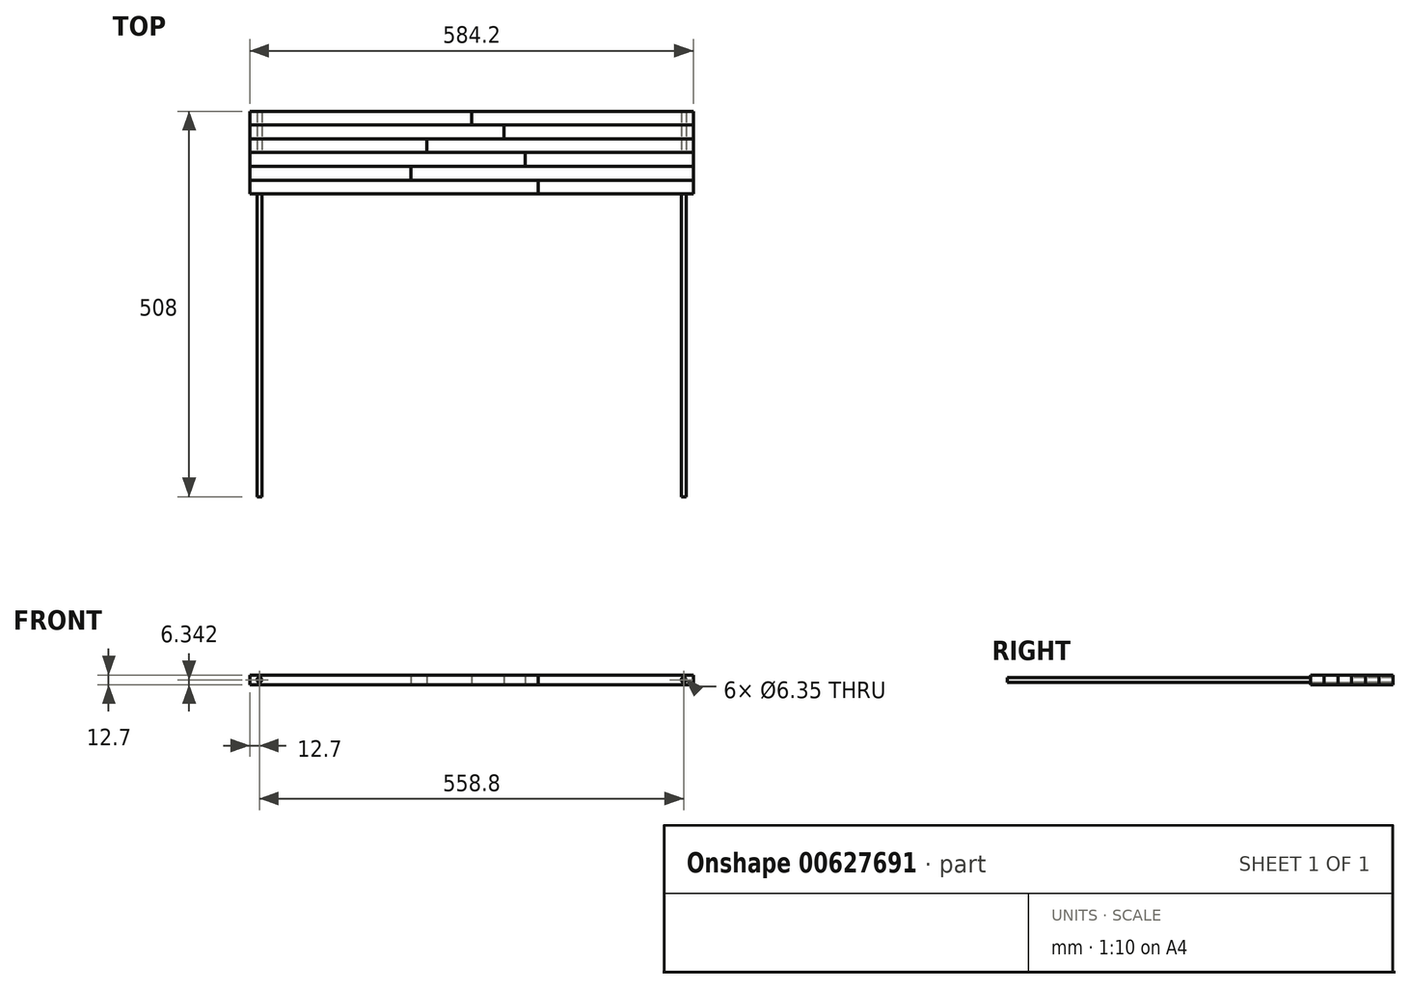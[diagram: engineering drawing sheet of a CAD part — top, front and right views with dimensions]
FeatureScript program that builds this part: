
annotation { "Feature Type Name" : "Feature", "Feature Type Description" : "" }
export const myFeature = defineFeature(function(context is Context, id is Id, definition is map)
    precondition{}
    {
        {
            var Q0;
            Q0=qCreatedBy(makeId("Top.planeOp"),FACE);
            var sketch = newSketch(context, id + "F0", { "sketchPlane" : qUnion([Q0])});
            skLineSegment(sketch, "E0.bottom", {"start": v(292.1, 254) * mm, "end": v(-292.1, 254) * mm});
            skLineSegment(sketch, "E0.top", {"start": v(292.1, -254) * mm, "end": v(-292.1, -254) * mm});
            skLineSegment(sketch, "E0.left", {"start": v(292.1, 254) * mm, "end": v(292.1, -254) * mm});
            skLineSegment(sketch, "E0.right", {"start": v(-292.1, 254) * mm, "end": v(-292.1, -254) * mm});
            skPoint(sketch, "E0.middle", {"position": v(0, 0) * mm});
            skLineSegment(sketch, "E1.1.0.0", {"start": v(292.1, 235.86) * mm, "end": v(-292.1, 235.86) * mm});
            skLineSegment(sketch, "E1.2.0.0", {"start": v(292.1, 217.71) * mm, "end": v(-292.1, 217.71) * mm});
            skLineSegment(sketch, "E1.3.0.0", {"start": v(292.1, 199.57) * mm, "end": v(-292.1, 199.57) * mm});
            skLineSegment(sketch, "E1.4.0.0", {"start": v(292.1, 181.43) * mm, "end": v(-292.1, 181.43) * mm});
            skLineSegment(sketch, "E1.5.0.0", {"start": v(292.1, 163.29) * mm, "end": v(-292.1, 163.29) * mm});
            skLineSegment(sketch, "E1.6.0.0", {"start": v(292.1, 145.14) * mm, "end": v(-292.1, 145.14) * mm});
            skLineSegment(sketch, "E1.7.0.0", {"start": v(292.1, 127) * mm, "end": v(-292.1, 127) * mm});
            skLineSegment(sketch, "E1.8.0.0", {"start": v(292.1, 108.86) * mm, "end": v(-292.1, 108.86) * mm});
            skLineSegment(sketch, "E1.9.0.0", {"start": v(292.1, 90.71) * mm, "end": v(-292.1, 90.71) * mm});
            skLineSegment(sketch, "E1.10.0.0", {"start": v(292.1, 72.57) * mm, "end": v(-292.1, 72.57) * mm});
            skLineSegment(sketch, "E1.11.0.0", {"start": v(292.1, 54.43) * mm, "end": v(-292.1, 54.43) * mm});
            skLineSegment(sketch, "E1.12.0.0", {"start": v(292.1, 36.29) * mm, "end": v(-292.1, 36.29) * mm});
            skLineSegment(sketch, "E1.13.0.0", {"start": v(292.1, 18.14) * mm, "end": v(-292.1, 18.14) * mm});
            skLineSegment(sketch, "E1.14.0.0", {"start": v(292.1, 0) * mm, "end": v(-292.1, 0) * mm});
            skLineSegment(sketch, "E1.15.0.0", {"start": v(292.1, -18.14) * mm, "end": v(-292.1, -18.14) * mm});
            skLineSegment(sketch, "E1.16.0.0", {"start": v(292.1, -36.29) * mm, "end": v(-292.1, -36.29) * mm});
            skLineSegment(sketch, "E1.17.0.0", {"start": v(292.1, -54.43) * mm, "end": v(-292.1, -54.43) * mm});
            skLineSegment(sketch, "E1.18.0.0", {"start": v(292.1, -72.57) * mm, "end": v(-292.1, -72.57) * mm});
            skLineSegment(sketch, "E1.19.0.0", {"start": v(292.1, -90.71) * mm, "end": v(-292.1, -90.71) * mm});
            skLineSegment(sketch, "E1.20.0.0", {"start": v(292.1, -108.86) * mm, "end": v(-292.1, -108.86) * mm});
            skLineSegment(sketch, "E1.21.0.0", {"start": v(292.1, -127) * mm, "end": v(-292.1, -127) * mm});
            skLineSegment(sketch, "E1.22.0.0", {"start": v(292.1, -145.14) * mm, "end": v(-292.1, -145.14) * mm});
            skLineSegment(sketch, "E1.23.0.0", {"start": v(292.1, -163.29) * mm, "end": v(-292.1, -163.29) * mm});
            skLineSegment(sketch, "E1.24.0.0", {"start": v(292.1, -181.43) * mm, "end": v(-292.1, -181.43) * mm});
            skLineSegment(sketch, "E1.25.0.0", {"start": v(292.1, -199.57) * mm, "end": v(-292.1, -199.57) * mm});
            skLineSegment(sketch, "E1.26.0.0", {"start": v(292.1, -217.71) * mm, "end": v(-292.1, -217.71) * mm});
            skLineSegment(sketch, "E1.27.0.0", {"start": v(292.1, -235.86) * mm, "end": v(-292.1, -235.86) * mm});
            skLineSegment(sketch, "E1.direction1", {"start": v(-292.1, 254) * mm, "end": v(-292.1, 235.86) * mm, "construction": true});
            skEllipse(sketch, "E2", {"center": v(0, 0) * mm, "majorRadius": 254 * mm, "minorRadius": 114.3 * mm, "majorAxis": v(0, 1), "construction": true});
            skLineSegment(sketch, "E3", {"start": v(0, 254) * mm, "end": v(0, 235.86) * mm});
            skLineSegment(sketch, "E4", {"start": v(42.42, 235.86) * mm, "end": v(42.42, 217.71) * mm});
            skLineSegment(sketch, "E5", {"start": v(-58.87, 217.71) * mm, "end": v(-58.87, 199.57) * mm});
            skLineSegment(sketch, "E6", {"start": v(70.7, 199.57) * mm, "end": v(70.7, 181.43) * mm});
            skLineSegment(sketch, "E7", {"start": v(-80, 181.43) * mm, "end": v(-80, 163.29) * mm});
            skLineSegment(sketch, "E8", {"start": v(87.55, 163.29) * mm, "end": v(87.55, 145.14) * mm});
            skLineSegment(sketch, "E9", {"start": v(-93.8, 145.14) * mm, "end": v(-93.8, 127) * mm});
            skLineSegment(sketch, "E10", {"start": v(98.99, 127) * mm, "end": v(98.99, 108.86) * mm});
            skLineSegment(sketch, "E11", {"start": v(-103.27, 108.86) * mm, "end": v(-103.27, 90.71) * mm});
            skLineSegment(sketch, "E12", {"start": v(106.76, 90.71) * mm, "end": v(106.76, 72.57) * mm});
            skLineSegment(sketch, "E13", {"start": v(-109.54, 72.57) * mm, "end": v(-109.54, 54.43) * mm});
            skLineSegment(sketch, "E14", {"start": v(111.64, 54.43) * mm, "end": v(111.64, 36.29) * mm});
            skLineSegment(sketch, "E15", {"start": v(-113.13, 36.29) * mm, "end": v(-113.13, 18.14) * mm});
            skLineSegment(sketch, "E16", {"start": v(114, 18.14) * mm, "end": v(114, 0) * mm});
            skLineSegment(sketch, "E17", {"start": v(-113.13, -18.14) * mm, "end": v(-113.13, 0) * mm});
            skLineSegment(sketch, "E18", {"start": v(113.13, -36.29) * mm, "end": v(113.13, -18.14) * mm});
            skLineSegment(sketch, "E19", {"start": v(-111.64, -54.43) * mm, "end": v(-111.64, -36.29) * mm});
            skLineSegment(sketch, "E20", {"start": v(-111.64, -36.29) * mm, "end": v(-110.28, -36.76) * mm});
            skLineSegment(sketch, "E21", {"start": v(109.54, -72.57) * mm, "end": v(109.54, -54.43) * mm});
            skLineSegment(sketch, "E22", {"start": v(-106.76, -90.71) * mm, "end": v(-106.76, -72.57) * mm});
            skLineSegment(sketch, "E23", {"start": v(-106.76, -72.57) * mm, "end": v(-105.46, -71.48) * mm});
            skLineSegment(sketch, "E24", {"start": v(103.27, -108.86) * mm, "end": v(103.27, -90.71) * mm});
            skLineSegment(sketch, "E25", {"start": v(-98.99, -127) * mm, "end": v(-98.99, -108.86) * mm});
            skLineSegment(sketch, "E26", {"start": v(93.8, -145.14) * mm, "end": v(93.8, -127) * mm});
            skLineSegment(sketch, "E27", {"start": v(93.8, -127) * mm, "end": v(95, -127.48) * mm});
            skLineSegment(sketch, "E28", {"start": v(-87.55, -163.29) * mm, "end": v(-87.55, -145.14) * mm});
            skLineSegment(sketch, "E29", {"start": v(80, -181.43) * mm, "end": v(80, -163.29) * mm});
            skLineSegment(sketch, "E30", {"start": v(-70.7, -199.57) * mm, "end": v(-70.7, -181.43) * mm});
            skLineSegment(sketch, "E31", {"start": v(58.87, -217.71) * mm, "end": v(58.87, -199.57) * mm});
            skLineSegment(sketch, "E32", {"start": v(-42.42, -235.86) * mm, "end": v(-42.42, -217.71) * mm});
            skLineSegment(sketch, "E33", {"start": v(0, -254) * mm, "end": v(0, -235.86) * mm});
            skSolve(sketch);
        }
        {
            var Q0;
            {var subQ3=sQuery(id+"F0.wireOp",EDGE,"E3");Q0=makeQuery(id+"F0.imprint","IMPRINT",FACE,{"disambiguationData":[TD([[makeQuery(id+"F0.imprint","IMPRINT",EDGE,{"derivedFrom":subQ3}),-1.0]])]});}
            extrude(context, id + "F1", {"entities" : qUnion([Q0]), "depth" : 12.7 * mm, "offsetDistance" : 25.4 * mm});
        }
        {
            var Q0;
            {var subQ0=sQuery(id+"F0.wireOp",EDGE,"E4");Q0=makeQuery(id+"F0.imprint","IMPRINT",FACE,{"disambiguationData":[TD([[makeQuery(id+"F0.imprint","IMPRINT",EDGE,{"derivedFrom":subQ0}),-1.0]])]});}
            extrude(context, id + "F2", {"entities" : qUnion([Q0]), "depth" : 12.7 * mm, "offsetDistance" : 25.4 * mm});
        }
        {
            var Q0;
            {var subQ5=sQuery(id+"F0.wireOp",EDGE,"E5");Q0=makeQuery(id+"F0.imprint","IMPRINT",FACE,{"disambiguationData":[TD([[makeQuery(id+"F0.imprint","IMPRINT",EDGE,{"derivedFrom":subQ5}),-1.0]])]});}
            extrude(context, id + "F3", {"entities" : qUnion([Q0]), "depth" : 12.7 * mm, "offsetDistance" : 25.4 * mm});
        }
        {
            var Q0;
            {var subQ0=sQuery(id+"F0.wireOp",EDGE,"E3");Q0=makeQuery(id+"F0.imprint","IMPRINT",FACE,{"disambiguationData":[TD([[makeQuery(id+"F0.imprint","IMPRINT",EDGE,{"derivedFrom":subQ0}),1.0]])]});}
            extrude(context, id + "F4", {"entities" : qUnion([Q0]), "depth" : 12.7 * mm, "offsetDistance" : 25.4 * mm});
        }
        {
            var Q0;
            {var subQ5=sQuery(id+"F0.wireOp",EDGE,"E4");Q0=makeQuery(id+"F0.imprint","IMPRINT",FACE,{"disambiguationData":[TD([[makeQuery(id+"F0.imprint","IMPRINT",EDGE,{"derivedFrom":subQ5}),1.0]])]});}
            extrude(context, id + "F5", {"entities" : qUnion([Q0]), "depth" : 12.7 * mm, "offsetDistance" : 25.4 * mm});
        }
        {
            var Q0;
            {var subQ2=sQuery(id+"F0.wireOp",EDGE,"E5");Q0=makeQuery(id+"F0.imprint","IMPRINT",FACE,{"disambiguationData":[TD([[makeQuery(id+"F0.imprint","IMPRINT",EDGE,{"derivedFrom":subQ2}),1.0]])]});}
            extrude(context, id + "F6", {"entities" : qUnion([Q0]), "depth" : 12.7 * mm, "offsetDistance" : 25.4 * mm});
        }
        {
            var Q0;
            Q0=qCreatedBy(makeId("Front.planeOp"),FACE);
            var sketch = newSketch(context, id + "F7", { "sketchPlane" : qUnion([Q0])});
            skCircle(sketch, "E34", {"center": v(-279.4, 6.34) * mm, "radius": 3.18 * mm});
            skCircle(sketch, "E35", {"center": v(279.4, 6.34) * mm, "radius": 3.18 * mm});
            skSolve(sketch);
        }
        {
            var Q0;
            Q0=makeQuery(id+"F7.imprint","IMPRINT",FACE,{"disambiguationData":[TD([[makeQuery(id+"F7.imprint","IMPRINT",EDGE,{"derivedFrom":sQuery(id+"F7.wireOp",EDGE,"E34")}),1.0]])]});
            var Q1;
            Q1=makeQuery(id+"F7.imprint","IMPRINT",FACE,{"disambiguationData":[TD([[makeQuery(id+"F7.imprint","IMPRINT",EDGE,{"derivedFrom":sQuery(id+"F7.wireOp",EDGE,"E35")}),1.0]])]});
            extrude(context, id + "F8", {"entities" : qUnion([Q0, Q1]), "endBound" : BoundingType.SYMMETRIC, "oppositeDirection" : true, "depth" : 508 * mm, "offsetDistance" : 25.4 * mm});
        }
        {
            var Q0;
            Q0=makeQuery(id+"F8.opExtrude","SWEPT_BODY",BODY,{"disambiguationData":[OSD([sQuery(id+"F7.wireOp",EDGE,"E34")])]});
            var Q1;
            Q1=makeQuery(id+"F8.opExtrude","SWEPT_BODY",BODY,{"disambiguationData":[OSD([sQuery(id+"F7.wireOp",EDGE,"E35")])]});
            var Q2;
            Q2=makeQuery(id+"F3.opExtrude","SWEPT_BODY",BODY,{"disambiguationData":[OSD([sQuery(id+"F0.wireOp",EDGE,"E0.right"),sQuery(id+"F0.wireOp",EDGE,"E1.2.0.0"),sQuery(id+"F0.wireOp",EDGE,"E1.3.0.0"),sQuery(id+"F0.wireOp",EDGE,"E5")])]});
            var Q3;
            Q3=makeQuery(id+"F2.opExtrude","SWEPT_BODY",BODY,{"disambiguationData":[OSD([sQuery(id+"F0.wireOp",EDGE,"E0.right"),sQuery(id+"F0.wireOp",EDGE,"E1.1.0.0"),sQuery(id+"F0.wireOp",EDGE,"E1.2.0.0"),sQuery(id+"F0.wireOp",EDGE,"E4")])]});
            var Q4;
            Q4=makeQuery(id+"F1.opExtrude","SWEPT_BODY",BODY,{"disambiguationData":[OSD([sQuery(id+"F0.wireOp",EDGE,"E0.bottom"),sQuery(id+"F0.wireOp",EDGE,"E0.right"),sQuery(id+"F0.wireOp",EDGE,"E1.1.0.0"),sQuery(id+"F0.wireOp",EDGE,"E3")])]});
            var Q5;
            Q5=makeQuery(id+"F6.opExtrude","SWEPT_BODY",BODY,{"disambiguationData":[OSD([sQuery(id+"F0.wireOp",EDGE,"E0.left"),sQuery(id+"F0.wireOp",EDGE,"E1.2.0.0"),sQuery(id+"F0.wireOp",EDGE,"E1.3.0.0"),sQuery(id+"F0.wireOp",EDGE,"E5")])]});
            var Q6;
            Q6=makeQuery(id+"F5.opExtrude","SWEPT_BODY",BODY,{"disambiguationData":[OSD([sQuery(id+"F0.wireOp",EDGE,"E0.left"),sQuery(id+"F0.wireOp",EDGE,"E1.1.0.0"),sQuery(id+"F0.wireOp",EDGE,"E1.2.0.0"),sQuery(id+"F0.wireOp",EDGE,"E4")])]});
            var Q7;
            Q7=makeQuery(id+"F4.opExtrude","SWEPT_BODY",BODY,{"disambiguationData":[OSD([sQuery(id+"F0.wireOp",EDGE,"E0.bottom"),sQuery(id+"F0.wireOp",EDGE,"E0.left"),sQuery(id+"F0.wireOp",EDGE,"E1.1.0.0"),sQuery(id+"F0.wireOp",EDGE,"E3")])]});
            booleanBodies(context, id + "F9", {"operationType" : BooleanOperationType.SUBTRACTION, "tools" : qUnion([Q0, Q1]), "targets" : qUnion([Q2, Q3, Q4, Q5, Q6, Q7])});
        }
        {
            var Q0;
            Q0 = qSketchRegion(id + "F7", true);
            extrude(context, id + "F10", {"entities" : qUnion([Q0]), "endBound" : BoundingType.SYMMETRIC, "depth" : 508 * mm, "offsetDistance" : 25.4 * mm});
        }
        {
            var Q0;
            {var subQ6=sQuery(id+"F0.wireOp",EDGE,"E6");Q0=makeQuery(id+"F0.imprint","IMPRINT",FACE,{"disambiguationData":[TD([[makeQuery(id+"F0.imprint","IMPRINT",EDGE,{"derivedFrom":subQ6}),-1.0]])]});}
            extrude(context, id + "F11", {"entities" : qUnion([Q0]), "depth" : 12.7 * mm, "offsetDistance" : 25.4 * mm});
        }
        {
            var Q0;
            {var subQ5=sQuery(id+"F0.wireOp",EDGE,"E6");Q0=makeQuery(id+"F0.imprint","IMPRINT",FACE,{"disambiguationData":[TD([[makeQuery(id+"F0.imprint","IMPRINT",EDGE,{"derivedFrom":subQ5}),1.0]])]});}
            extrude(context, id + "F12", {"entities" : qUnion([Q0]), "depth" : 12.7 * mm, "offsetDistance" : 25.4 * mm});
        }
        {
            var Q0;
            {var subQ5=sQuery(id+"F0.wireOp",EDGE,"E7");Q0=makeQuery(id+"F0.imprint","IMPRINT",FACE,{"disambiguationData":[TD([[makeQuery(id+"F0.imprint","IMPRINT",EDGE,{"derivedFrom":subQ5}),-1.0]])]});}
            extrude(context, id + "F13", {"entities" : qUnion([Q0]), "depth" : 12.7 * mm, "offsetDistance" : 25.4 * mm});
        }
        {
            var Q0;
            {var subQ6=sQuery(id+"F0.wireOp",EDGE,"E7");Q0=makeQuery(id+"F0.imprint","IMPRINT",FACE,{"disambiguationData":[TD([[makeQuery(id+"F0.imprint","IMPRINT",EDGE,{"derivedFrom":subQ6}),1.0]])]});}
            extrude(context, id + "F14", {"entities" : qUnion([Q0]), "depth" : 12.7 * mm, "offsetDistance" : 25.4 * mm});
        }
        {
            var Q0;
            {var subQ0=sQuery(id+"F0.wireOp",EDGE,"E8");Q0=makeQuery(id+"F0.imprint","IMPRINT",FACE,{"disambiguationData":[TD([[makeQuery(id+"F0.imprint","IMPRINT",EDGE,{"derivedFrom":subQ0}),-1.0]])]});}
            extrude(context, id + "F15", {"entities" : qUnion([Q0]), "depth" : 12.7 * mm, "offsetDistance" : 25.4 * mm});
        }
        {
            var Q0;
            {var subQ5=sQuery(id+"F0.wireOp",EDGE,"E8");Q0=makeQuery(id+"F0.imprint","IMPRINT",FACE,{"disambiguationData":[TD([[makeQuery(id+"F0.imprint","IMPRINT",EDGE,{"derivedFrom":subQ5}),1.0]])]});}
            extrude(context, id + "F16", {"entities" : qUnion([Q0]), "depth" : 12.7 * mm, "offsetDistance" : 25.4 * mm});
        }
    });
